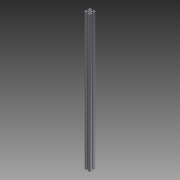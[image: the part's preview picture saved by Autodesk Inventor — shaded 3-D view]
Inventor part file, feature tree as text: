
AUTODESK INVENTOR PART (.ipt)
format: ipt  version: 2016 (Build 200138000, 138)  size: 214,016 bytes
history: native  units: mm
features: other x42, sketch x5, hole x4, extrude x1
ambient origin geometry x8: Origin, YZ Plane, XZ Plane, XY Plane, X Axis, Y Axis, Z Axis, Center Point
bodies: Solid1 (feature_tree)
feature tree (52):
  extrude  "Extrusion1"  [1 undecoded]
  hole  "Drilling 1"  [1 undecoded]
  hole  "Drilling 2"  [1 undecoded]
  hole  "Drilling 3"  [1 undecoded]
  hole  "Drilling 4"  [1 undecoded]
  other  "side_4d_XY"
  other  "side_4d_YZ"
  other  "side_4d_ZX"
  other  "side_4d_X"
  other  "side_4d_Y"
  other  "side_4d_Z"
  other  "side_4d_Center"
  other  "side_1a_XY"
  other  "side_1a_YZ"
  other  "side_1a_ZX"
  other  "side_1a_X"
  other  "side_1a_Y"
  other  "side_1a_Z"
  other  "side_1a_Center"
  other  "side_2b_XY"
  other  "side_2b_YZ"
  other  "side_2b_ZX"
  other  "side_2b_X"
  other  "side_2b_Y"
  other  "side_2b_Z"
  other  "side_2b_Center"
  other  "side_3c_XY"
  other  "side_3c_YZ"
  other  "side_3c_ZX"
  other  "side_3c_X"
  other  "side_3c_Y"
  other  "side_3c_Z"
  other  "side_3c_Center"
  other  "end_XY"
  other  "end_YZ"
  other  "end_ZX"
  other  "end_X"
  other  "end_Y"
  other  "end_Z"
  other  "end_Center"
  other  "start_XY"
  other  "start_YZ"
  other  "start_ZX"
  other  "start_X"
  other  "start_Y"
  other  "start_Z"
  other  "start_Center"
  sketch  "Skizze_1"  dims[d0=950.0mm d1=0.0mm]
  sketch  "Sketch2"  dims[d2=5.0mm d3=6.0mm d4=4.0mm d5=2.0mm d6=90.0deg d7=6000.0mm d8=0.0mm]
  sketch  "Sketch3"  dims[d9=5.0mm d10=6.0mm d11=4.0mm d12=2.0mm d13=90.0deg d14=6000.0mm d15=0.0mm]
  sketch  "Sketch4"  dims[d16=5.0mm d17=6.0mm d18=4.0mm d19=2.0mm d20=90.0deg d21=6000.0mm d22=0.0mm]
  sketch  "Sketch5"  dims[d23=5.0mm d24=6.0mm d25=4.0mm d26=2.0mm d27=90.0deg d28=6000.0mm d29=0.0mm]
note: 5 required parameter values undecoded (feature->parameter linkage not recoverable at this tier; creation-order binding heuristic only, values carry confidence <= 0.55)
